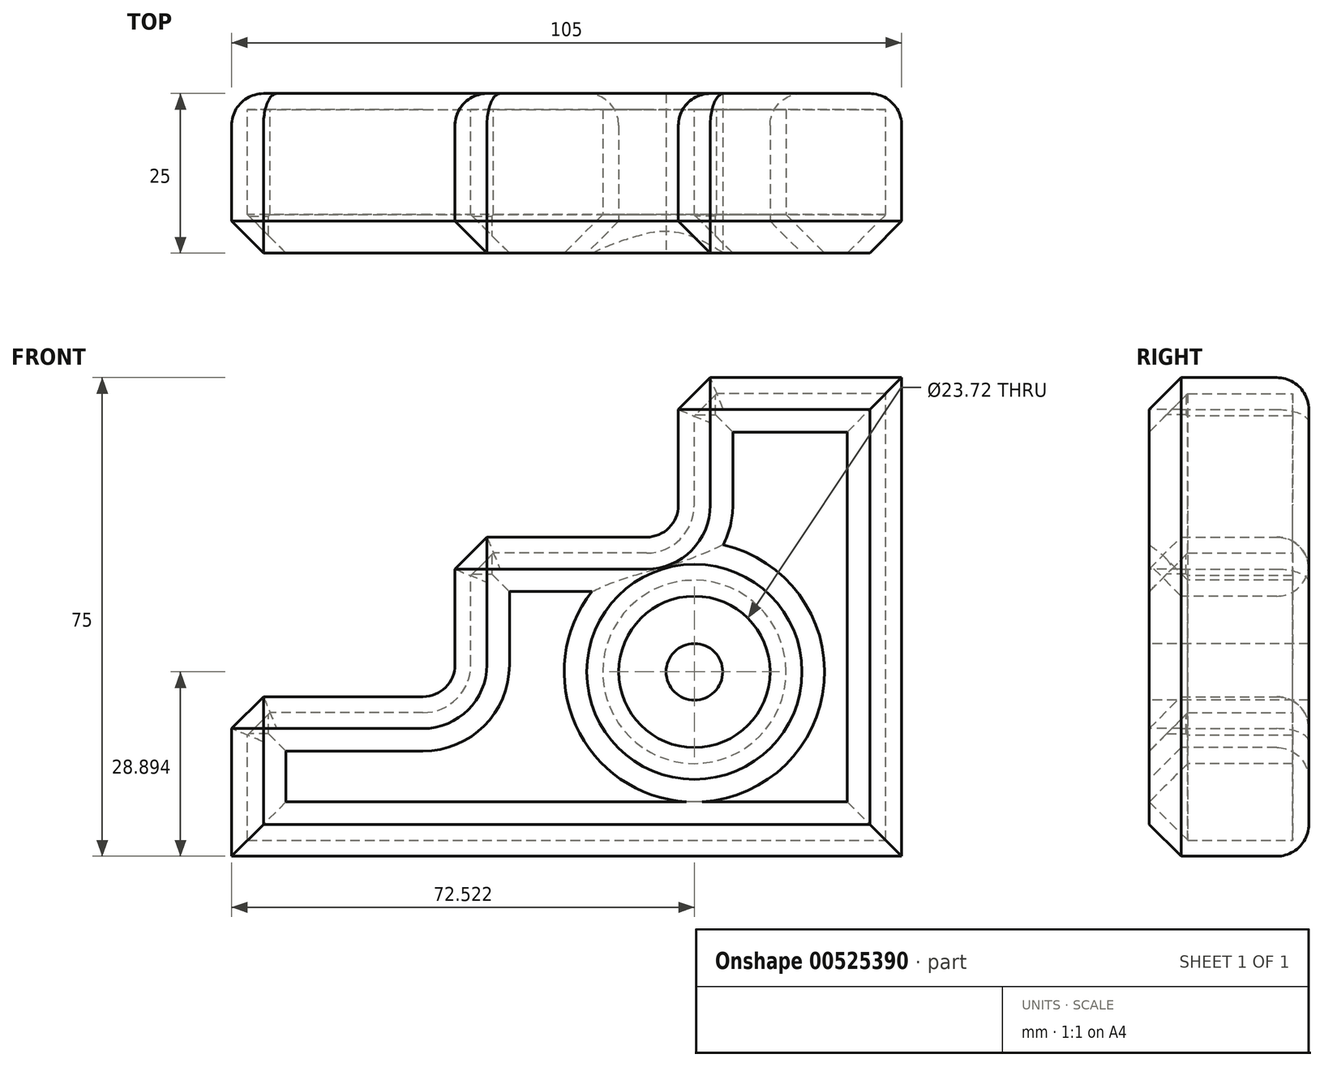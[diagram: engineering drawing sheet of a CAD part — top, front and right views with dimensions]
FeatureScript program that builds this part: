
annotation { "Feature Type Name" : "Feature", "Feature Type Description" : "" }
export const myFeature = defineFeature(function(context is Context, id is Id, definition is map)
    precondition{}
    {
        {
            var Q0;
            Q0=qCreatedBy(makeId("Front.planeOp"),FACE);
            var sketch = newSketch(context, id + "F0", { "sketchPlane" : qUnion([Q0])});
            skLineSegment(sketch, "E0", {"start": v(56, 0) * mm, "end": v(56, 75) * mm});
            skLineSegment(sketch, "E1", {"start": v(56, 75) * mm, "end": v(21, 75) * mm});
            skLineSegment(sketch, "E2", {"start": v(21, 75) * mm, "end": v(21, 55) * mm});
            skLineSegment(sketch, "E3", {"start": v(16, 50) * mm, "end": v(-14, 50) * mm});
            skLineSegment(sketch, "E4", {"start": v(-14, 50) * mm, "end": v(-14, 30) * mm});
            skLineSegment(sketch, "E5", {"start": v(-19, 25) * mm, "end": v(-49, 25) * mm});
            skLineSegment(sketch, "E6", {"start": v(-49, 25) * mm, "end": v(-49, 0) * mm});
            skLineSegment(sketch, "E7", {"start": v(-49, 0) * mm, "end": v(56, 0) * mm});
            skPoint(sketch, "E8.visualSharp", {"position": v(21, 50) * mm});
            skArc(sketch, "E8.filletArc", {"start": v(16, 50) * mm, "mid": v(19.53, 51.46) * mm, "end": v(21, 55) * mm});
            skPoint(sketch, "E9.visualSharp", {"position": v(-14, 25) * mm});
            skArc(sketch, "E9.filletArc", {"start": v(-19, 25) * mm, "mid": v(-15.47, 26.46) * mm, "end": v(-14, 30) * mm});
            skSolve(sketch);
        }
        {
            var Q0;
            Q0 = qSketchRegion(id + "F0", true);
            var Q1;
            Q1 = qConstructionFilter(qBodyType(qCreatedBy(id + "F0" ,EDGE), BodyType.WIRE), ConstructionObject.NO);
            extrude(context, id + "F1", {"entities" : qUnion([Q0]), "surfaceEntities" : qUnion([Q1]), "depth" : 25 * mm, "offsetDistance" : 25 * mm});
        }
        {
            var Q0;
            Q0=makeQuery(id+"F1.opExtrude","CAP_FACE",FACE,{"disambiguationData":[OSD([sQuery(id+"F0.wireOp",EDGE,"E0"),sQuery(id+"F0.wireOp",EDGE,"E1"),sQuery(id+"F0.wireOp",EDGE,"E2"),sQuery(id+"F0.wireOp",EDGE,"E3"),sQuery(id+"F0.wireOp",EDGE,"E4"),sQuery(id+"F0.wireOp",EDGE,"E5"),sQuery(id+"F0.wireOp",EDGE,"E6"),sQuery(id+"F0.wireOp",EDGE,"E7"),sQuery(id+"F0.wireOp",EDGE,"E8.filletArc"),sQuery(id+"F0.wireOp",EDGE,"E9.filletArc")])],"isStart":false});
            var sketch = newSketch(context, id + "F2", { "sketchPlane" : qUnion([Q0])});
            skCircle(sketch, "E10", {"center": v(23.51, 28.9) * mm, "radius": 11.86 * mm});
            skCircle(sketch, "E11", {"center": v(23.51, 28.9) * mm, "radius": 4.43 * mm});
            skSolve(sketch);
        }
        {
            var Q0;
            Q0=makeQuery(id+"F2.imprint","IMPRINT",FACE,{"disambiguationData":[TD([[makeQuery(id+"F2.imprint","IMPRINT",EDGE,{"derivedFrom":sQuery(id+"F2.wireOp",EDGE,"E10")}),1.0]])]});
            extrude(context, id + "F3", {"entities" : qUnion([Q0]), "operationType" : NewBodyOperationType.REMOVE, "oppositeDirection" : true, "depth" : 30 * mm, "offsetDistance" : 25 * mm});
        }
        {
            var Q0;
            Q0=makeQuery(id+"F1.opExtrude","SWEPT_EDGE",EDGE,{"disambiguationData":[OSD([sQuery(id+"F0.wireOp",EDGE,"E3"),sQuery(id+"F0.wireOp",EDGE,"E4")])]});
            var Q1;
            Q1=makeQuery(id+"F1.opExtrude","SWEPT_EDGE",EDGE,{"disambiguationData":[OSD([sQuery(id+"F0.wireOp",EDGE,"E5"),sQuery(id+"F0.wireOp",EDGE,"E6")])]});
            var Q2;
            Q2=makeQuery(id+"F1.opExtrude","SWEPT_EDGE",EDGE,{"disambiguationData":[OSD([sQuery(id+"F0.wireOp",EDGE,"E1"),sQuery(id+"F0.wireOp",EDGE,"E2")])]});
            var Q3;
            {var subQ0=sQuery(id+"F0.wireOp",EDGE,"E8.filletArc");var subQ1=sQuery(id+"F0.wireOp",EDGE,"E7");var subQ2=sQuery(id+"F0.wireOp",EDGE,"E6");var subQ3=sQuery(id+"F0.wireOp",EDGE,"E5");var subQ4=sQuery(id+"F0.wireOp",EDGE,"E4");var subQ5=sQuery(id+"F0.wireOp",EDGE,"E9.filletArc");var subQ6=sQuery(id+"F0.wireOp",EDGE,"E0");var subQ7=sQuery(id+"F0.wireOp",EDGE,"E3");var subQ8=sQuery(id+"F0.wireOp",EDGE,"E1");var subQ9=sQuery(id+"F0.wireOp",EDGE,"E2");Q3=makeQuery(id+"F3.boolean.opBoolean","SPLIT",FACE,{"disambiguationData":[TD([makeQuery(id+"F1.opExtrude","SWEPT_FACE",FACE,{"disambiguationData":[OSD([subQ6])]})])],"derivedFrom":makeQuery(id+"F1.opExtrude","CAP_FACE",FACE,{"disambiguationData":[OSD([subQ6,subQ8,subQ9,subQ7,subQ4,subQ3,subQ2,subQ1,subQ0,subQ5])],"isStart":false})});}
            chamfer(context, id + "F4", {"entities" : qUnion([Q0, Q1, Q2, Q3]), "width" : 5 * mm, "tangentPropagation" : true});
        }
        {
            var Q0;
            {var subQ0=sQuery(id+"F0.wireOp",EDGE,"E8.filletArc");var subQ1=sQuery(id+"F0.wireOp",EDGE,"E7");var subQ2=sQuery(id+"F0.wireOp",EDGE,"E6");var subQ3=sQuery(id+"F0.wireOp",EDGE,"E5");var subQ4=sQuery(id+"F0.wireOp",EDGE,"E4");var subQ5=sQuery(id+"F0.wireOp",EDGE,"E9.filletArc");var subQ6=sQuery(id+"F0.wireOp",EDGE,"E0");var subQ7=sQuery(id+"F0.wireOp",EDGE,"E3");var subQ8=sQuery(id+"F0.wireOp",EDGE,"E1");var subQ9=sQuery(id+"F0.wireOp",EDGE,"E2");Q0=makeQuery(id+"F3.boolean.opBoolean","SPLIT",FACE,{"disambiguationData":[TD([makeQuery(id+"F1.opExtrude","SWEPT_FACE",FACE,{"disambiguationData":[OSD([subQ6])]})])],"derivedFrom":makeQuery(id+"F1.opExtrude","CAP_FACE",FACE,{"disambiguationData":[OSD([subQ6,subQ8,subQ9,subQ7,subQ4,subQ3,subQ2,subQ1,subQ0,subQ5])],"isStart":false})});}
            shell(context, id + "F5", {"entities" : qUnion([Q0]), "thickness" : 2.5 * mm});
        }
        {
            var Q0;
            {var subQ0=sQuery(id+"F0.wireOp",EDGE,"E8.filletArc");var subQ1=sQuery(id+"F0.wireOp",EDGE,"E7");var subQ2=sQuery(id+"F0.wireOp",EDGE,"E6");var subQ3=sQuery(id+"F0.wireOp",EDGE,"E5");var subQ4=sQuery(id+"F0.wireOp",EDGE,"E4");var subQ5=sQuery(id+"F0.wireOp",EDGE,"E9.filletArc");var subQ6=sQuery(id+"F0.wireOp",EDGE,"E0");var subQ7=sQuery(id+"F0.wireOp",EDGE,"E3");var subQ8=sQuery(id+"F0.wireOp",EDGE,"E1");var subQ9=sQuery(id+"F0.wireOp",EDGE,"E2");Q0=makeQuery(id+"F3.boolean.opBoolean","SPLIT",FACE,{"disambiguationData":[TD([makeQuery(id+"F1.opExtrude","SWEPT_FACE",FACE,{"disambiguationData":[OSD([subQ6])]})])],"derivedFrom":makeQuery(id+"F1.opExtrude","CAP_FACE",FACE,{"disambiguationData":[OSD([subQ6,subQ8,subQ9,subQ7,subQ4,subQ3,subQ2,subQ1,subQ0,subQ5])],"isStart":true})});}
            fillet(context, id + "F6", {"entities" : qUnion([Q0]), "radius" : 5 * mm, "tangentPropagation" : true, "allowEdgeOverflow" : false});
        }
    });
